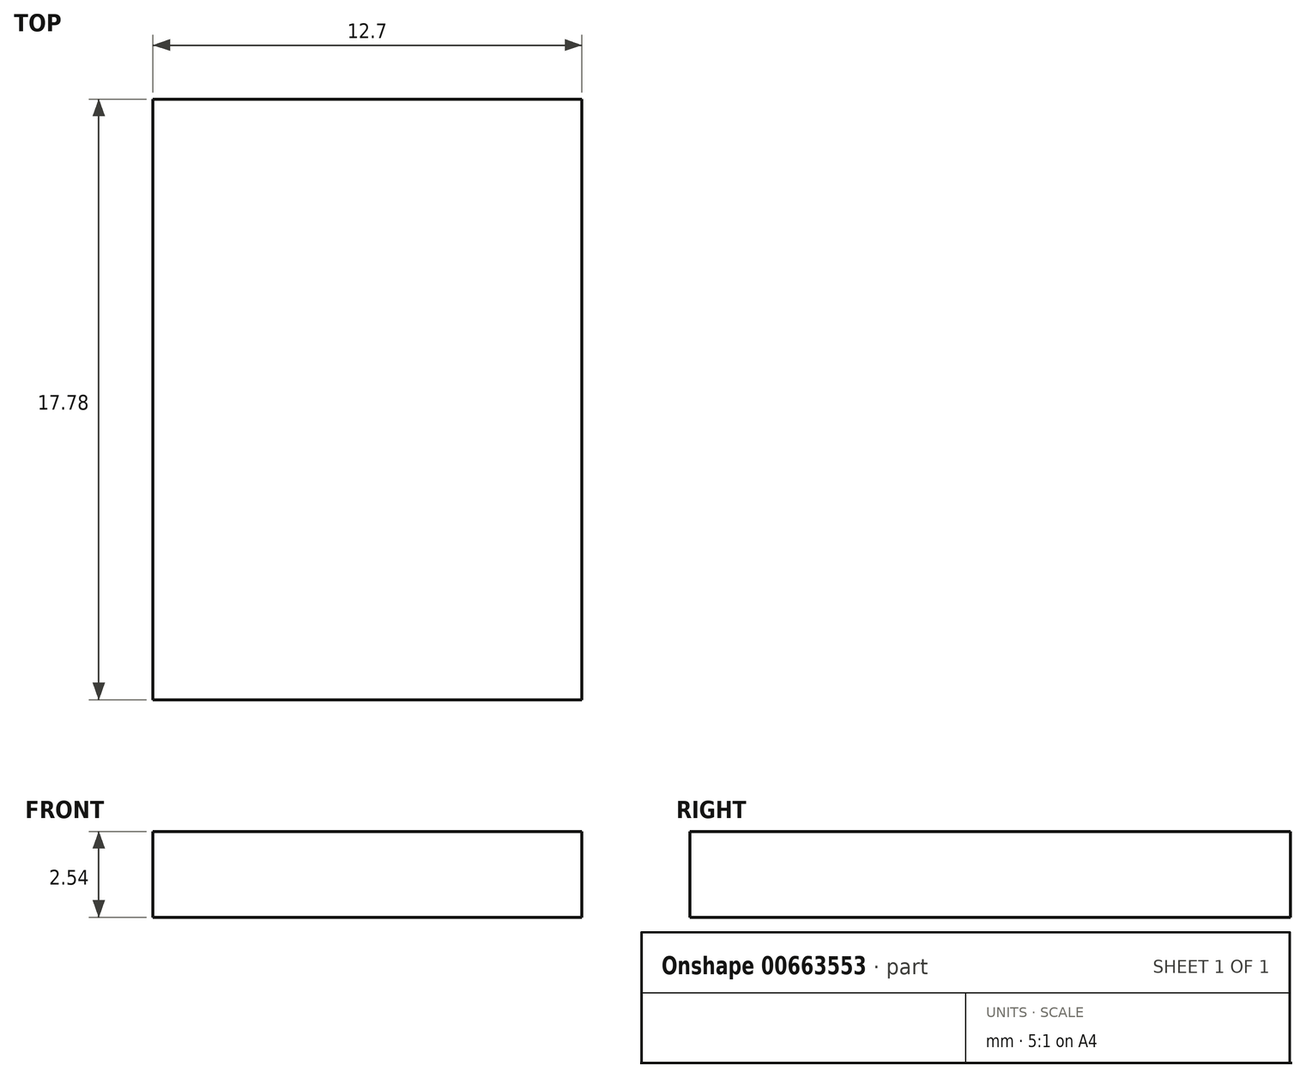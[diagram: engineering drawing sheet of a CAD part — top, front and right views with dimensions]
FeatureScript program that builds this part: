
annotation { "Feature Type Name" : "Feature", "Feature Type Description" : "" }
export const myFeature = defineFeature(function(context is Context, id is Id, definition is map)
    precondition{}
    {
        {
            var Q0;
            Q0=qCreatedBy(makeId("Front.planeOp"),FACE);
            var sketch = newSketch(context, id + "F0", { "sketchPlane" : qUnion([Q0])});
            skLineSegment(sketch, "E0.bottom", {"start": v(-6.35, -1.27) * mm, "end": v(6.35, -1.27) * mm});
            skLineSegment(sketch, "E0.top", {"start": v(-6.35, 1.27) * mm, "end": v(6.35, 1.27) * mm});
            skLineSegment(sketch, "E0.left", {"start": v(-6.35, -1.27) * mm, "end": v(-6.35, 1.27) * mm});
            skLineSegment(sketch, "E0.right", {"start": v(6.35, -1.27) * mm, "end": v(6.35, 1.27) * mm});
            skPoint(sketch, "E0.middle", {"position": v(0, 0) * mm});
            skSolve(sketch);
        }
        {
            var Q0;
            Q0 = qSketchRegion(id + "F0", true);
            extrude(context, id + "F1", {"entities" : qUnion([Q0]), "depth" : 17.78 * mm, "offsetDistance" : 25.4 * mm});
        }
    });
